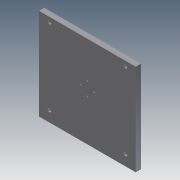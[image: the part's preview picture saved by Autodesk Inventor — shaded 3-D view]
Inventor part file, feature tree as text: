
AUTODESK INVENTOR PART (.ipt)
format: ipt  version: 2011 (Build 150239000, 239)  size: 197,120 bytes
history: native  units: in
note: dims shown in document units (in); Inventor stores cm internally (conversion verified against a paired STEP export)
features: extrude x14, sketch x14, fillet x1
ambient origin geometry x8: Origin, YZ Plane, XZ Plane, XY Plane, X Axis, Y Axis, Z Axis, Center Point
bodies: Solid1 (feature_tree)
feature tree (29):
  extrude  "Extrusion1"  Depth=4.0in
  extrude  "Extrusion2"  Depth=2.16in
  extrude  "Extrusion3"  Depth=1.7655in
  extrude  "Extrusion4"  Depth=0.029in TaperAngle=0.0deg
  extrude  "Extrusion5"  Depth=2.36in
  fillet  "Fillet1"  Radius=2.56in
  extrude  "Extrusion6"  Depth=0.125in
  extrude  "Extrusion7"  Depth=0.25in TaperAngle=0.0deg
  extrude  "Extrusion8"  Depth=0.25in
  extrude  "Extrusion9"  Depth=1.0in TaperAngle=0.0deg
  extrude  "Extrusion10"  Depth=0.25in TaperAngle=0.0deg
  extrude  "Extrusion11"  Depth=0.25in TaperAngle=0.0deg
  extrude  "Extrusion12"  Depth=0.6299in
  extrude  "Extrusion13"  Depth=0.0787in
  extrude  "Extrusion14"  Depth=0.0787in
  sketch  "Sketch1"  dims[d0=4.0in d1=4.0in]
  sketch  "Sketch2"  dims[d2=0.029in d3=0.0in d4=2.16in]
  sketch  "Sketch3"  dims[d5=0.029in d6=0.0in d7=1.7655in]
  sketch  "Sketch4"  dims[d8=0.156in d9=0.029in d10=0.0in]
  sketch  "Sketch5"  dims[d11=0.029in d12=0.0in d13=2.36in d14=2.56in]
  sketch  "Sketch6"  dims[d15=0.262in d16=0.0in d17=0.125in]
  sketch  "Sketch7"  dims[d18=0.25in d19=0.0in d20=0.25in d21=0.0in]
  sketch  "Sketch8"  dims[d22=0.25in d23=0.25in]
  sketch  "Sketch9"  dims[d24=0.5in d25=1.0in d26=0.0in]
  sketch  "Sketch10"  dims[d27=1.0in d28=0.0in d29=0.25in d30=0.0in]
  sketch  "Sketch11"  dims[d31=0.25in d32=0.0in d33=0.25in d34=0.0in]
  sketch  "Sketch12"  dims[d35=0.25in d36=0.0in d37=0.6299in]
  sketch  "Sketch13"  dims[d38=0.0787in d39=0.0787in]
  sketch  "Sketch14"  dims[d40=0.0787in d41=0.0787in d42=1.0in d43=0.0in]
